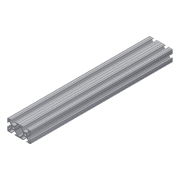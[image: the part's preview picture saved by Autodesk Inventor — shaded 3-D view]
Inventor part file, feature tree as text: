
AUTODESK INVENTOR PART (.ipt)
format: ipt  version: 2013 (Build 170138000, 138)  size: 306,176 bytes
history: native  units: in
note: dims shown in document units (in); Inventor stores cm internally (conversion verified against a paired STEP export)
features: other x3, extrude x1, sketch x1
ambient origin geometry x8: Origin, YZ Plane, XZ Plane, XY Plane, X Axis, Y Axis, Z Axis, Center Point
bodies: Solid1 (feature_tree)
feature tree (5):
  other  "Blocks"
  extrude  "Extrusion1"  [1 undecoded]
  sketch  "Sketch1"  dims[d1=0.0in]
  other  "1020 profile"
  other  "1020 profile:1"
note: 1 required parameter value undecoded (feature->parameter linkage not recoverable at this tier; creation-order binding heuristic only, values carry confidence <= 0.55)
